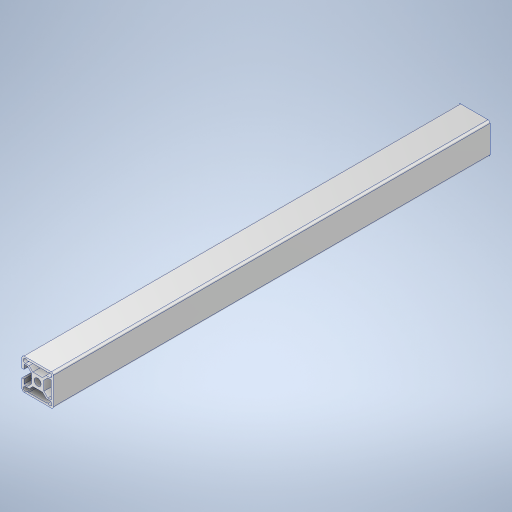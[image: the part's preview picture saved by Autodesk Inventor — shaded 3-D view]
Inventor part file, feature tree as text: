
AUTODESK INVENTOR PART (.ipt)
format: ipt  version: 2024 (Build 280153000, 153)  size: 370,688 bytes
history: native  units: mm
features: other x21, sketch x4, extrude x3, thread x2, hole x1
ambient origin geometry x8: Origin, YZ Plane, XZ Plane, XY Plane, X Axis, Y Axis, Z Axis, Center Point
bodies: Solid1 (feature_tree)
feature tree (31):
  extrude  "Extrusion1"  Depth=2.0mm TaperAngle=0.0deg
  hole  "Hole1"  [1 undecoded]
  extrude  "Extrusion2"  TaperAngle=0.0deg  [1 undecoded]
  extrude  "Extrusion3"  Depth=10.0mm TaperAngle=0.0deg
  other  "C1_XY"
  other  "C1_YZ"
  other  "C1_ZX"
  other  "C1_X"
  other  "C1_Y"
  other  "C1_Z"
  other  "C1_Center"
  other  "to_frame_cap1_XY"
  other  "to_frame_cap1_YZ"
  other  "to_frame_cap1_ZX"
  other  "to_frame_cap1_X"
  other  "to_frame_cap1_Y"
  other  "to_frame_cap1_Z"
  other  "to_frame_cap1_Center"
  other  "to_frame_cap2_XY"
  other  "to_frame_cap2_YZ"
  other  "to_frame_cap2_ZX"
  other  "to_frame_cap2_X"
  other  "to_frame_cap2_Y"
  other  "to_frame_cap2_Z"
  other  "to_frame_cap2_Center"
  thread  "Thread1"  [1 undecoded]
  thread  "Thread2"  [1 undecoded]
  sketch  "Sketch_122"  dims[d2=6.8mm d3=6.0mm d4=4.0mm d5=2.0mm d6=90.0deg d7=600.0mm d8=0.0mm d9=600.0mm d10=0.0mm]
  sketch  "Sketch2"  dims[d0=417.0mm d1=0.0mm]
  sketch  "Sketch_173"  dims[d11=600.0mm d12=0.0mm d13=0.0mm]
  sketch  "Sketch_174"  dims[d14=0.0mm d15=0.0mm d16=10.0mm d17=0.0mm d18=10.0mm d19=0.0mm]
note: 4 required parameter values undecoded (feature->parameter linkage not recoverable at this tier; creation-order binding heuristic only, values carry confidence <= 0.55)
